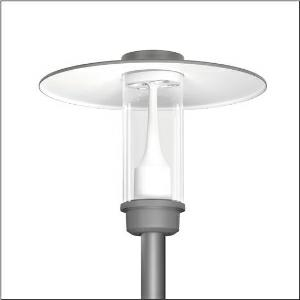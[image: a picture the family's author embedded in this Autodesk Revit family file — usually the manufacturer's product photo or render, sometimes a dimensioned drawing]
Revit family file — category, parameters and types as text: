
# Revit family: litepole_iq_2___p1_0a_5xa5425nf14h_b5d3
name_source: partatom
category: Lighting Fixtures
units: mm (PartAtom-declared; Revit-internal decimal feet)

## family parameters
Cut with Voids When Loaded = No
Host = Face
Light Source = No
Part Type = Normal
Room Calculation Point = No
Round Connector Dimension = Use Diameter
Shared = No

## types (1)
- --- (1 x LED, 1520 lm, 11.8 W, 2700K)
    Apparent Load = 12 VA
    CIE Flux Codes = 33 62 89 96 100
    Color Rendering = 70
    Color Temperature = 2700K
    Default Elevation = 1800 mm
    Description = Litepole iQ 2, mast luminaire, Module 540 iQ-SR, primary light control with 3 zone facetted reflector, of plastic, silver coated, highly specular, structured, primary optical cover: cover, of PMMA, transparent, light distribution: P1.0a, light emission: direct distribution, primary light characteristic: strongly asymmetric, installation type: post-top, LED, High Power LED, rated luminous flux: 1.520lm, luminous efficacy: 129lm/W, light colour: 727, colour temperature: 2700K, control gear: ECG iQ, control: presetting dimming logarithmic, Street-Remote, Auto-Match, Temp-Guard, Lumen-Switch, Night-Set, Smart-Wire, Light-Fading, Desk-Remote (wireless, voltage-free reading and setting of iQ features in the workshop via application-optimized NFC function/RFID function), optimised constant luminous flux control (CLO 2.0), with terminal, 6-pole, max. 2.5mm², mains connection: 220..240V, AC, 50/60Hz, start of lifetime: 12W, end of lifetime: 12W, reduction: 6W, luminaire housing, upper part, of aluminium, coated, Siteco® metallic grey (DB 702S), diameter: 750mm, height: 590mm, spigot size: d x l = 76 x 70mm (post-top) | with reducer (optional accessory) 60 x 70mm, post-top mast mounting element, of diecast aluminium, coated, Siteco® metallic grey (DB 702S), Module 540 iQ-SR, traffic white (RAL 9016), equipment: standard, protection rating (complete): IP65, insulation class (complete): insulation class II (safety insulation), certification: CE, ENEC, VDE, packaging unit: 1 piece

Light Distribution: P1.0a
    Height = 590 mm
    Lamp = 1 x LED
    Lamp Light Flux = 1520 lm
    Lamp Power = 11.8 W
    Lamp count = 1
    Length = 750 mm
    Luminous efficacy = 129 lm/W
    Manufacturer = Siteco
    ModVariant = No
    Model = 5XA5425NF14H
    Number of Poles = 1
    OnlyDefault = Yes
    Power Factor = 1
    Product Name = Litepole iQ 2 | P1.0a
    Product group = mast luminaire | pylon top
    ProductGroupID = 6100
    Protection Class = Protection class II
    Protection Degree = IP 65
    RLX_Detail_Level = 1
    RlxData = <blob elided: 138213 chars, md5=6332b0a5>
    Socket = socket
    Standby Power = 0 W
    System Light Flux = 1520 lm
    System Power = 12 W
    Type Comments = factory setting: luminous flux: 100 % | dim-lin: 254 | 472 mA
    Type Image = l_1006518.jpg
    URL = http://relux.com
    VarID = @adj_062243
    Voltage = 0 V
    Weight = 0.00 kg
    Width = 0 mm  [stored 0 ft]

note: [stored X ft] marks values corroborated as IEEE doubles in the binary element streams (Revit-internal decimal feet)

## geometry (parser evidence)
native form markers: Blend x4, Sweep x11
no freeform markers — native parametric forms only
